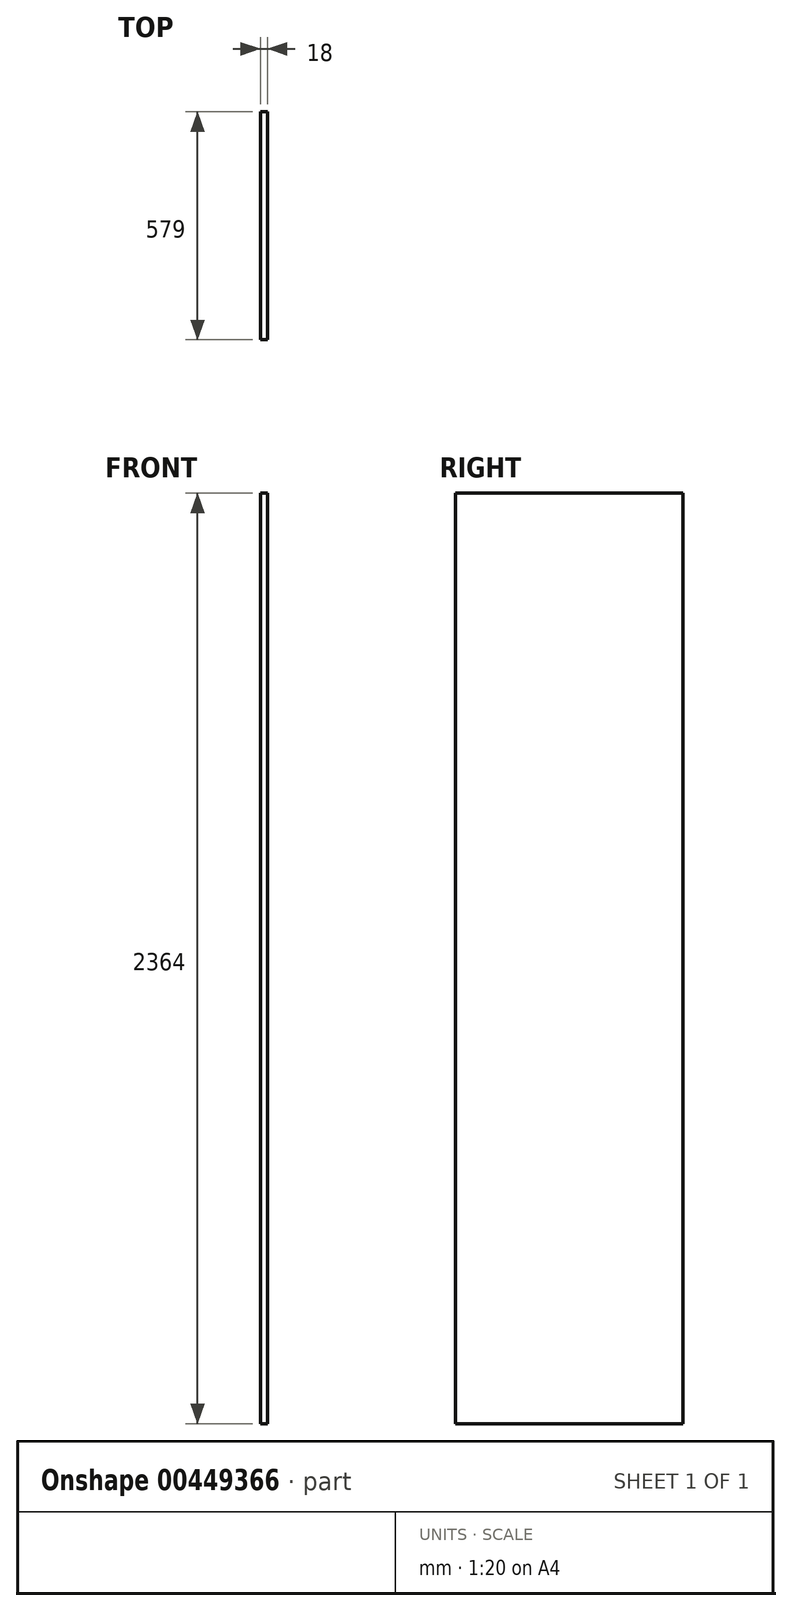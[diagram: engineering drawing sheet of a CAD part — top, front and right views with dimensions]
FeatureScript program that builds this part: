
annotation { "Feature Type Name" : "Feature", "Feature Type Description" : "" }
export const myFeature = defineFeature(function(context is Context, id is Id, definition is map)
    precondition{}
    {
        {
            var Q0;
            Q0=qCreatedBy(makeId("Right.planeOp"),FACE);
            var sketch = newSketch(context, id + "F0", { "sketchPlane" : qUnion([Q0])});
            skLineSegment(sketch, "E0.bottom", {"start": v(0, 2464) * mm, "end": v(579, 2464) * mm});
            skLineSegment(sketch, "E0.top", {"start": v(0, 100) * mm, "end": v(579, 100) * mm});
            skLineSegment(sketch, "E0.left", {"start": v(0, 2464) * mm, "end": v(0, 100) * mm});
            skLineSegment(sketch, "E0.right", {"start": v(579, 2464) * mm, "end": v(579, 100) * mm});
            skSolve(sketch);
        }
        {
            var Q0;
            Q0=qSketchRegion(id+"F0",true);
            extrude(context, id + "F1", {"entities" : qUnion([Q0]), "oppositeDirection" : true, "depth" : 18 * mm});
        }
    });
